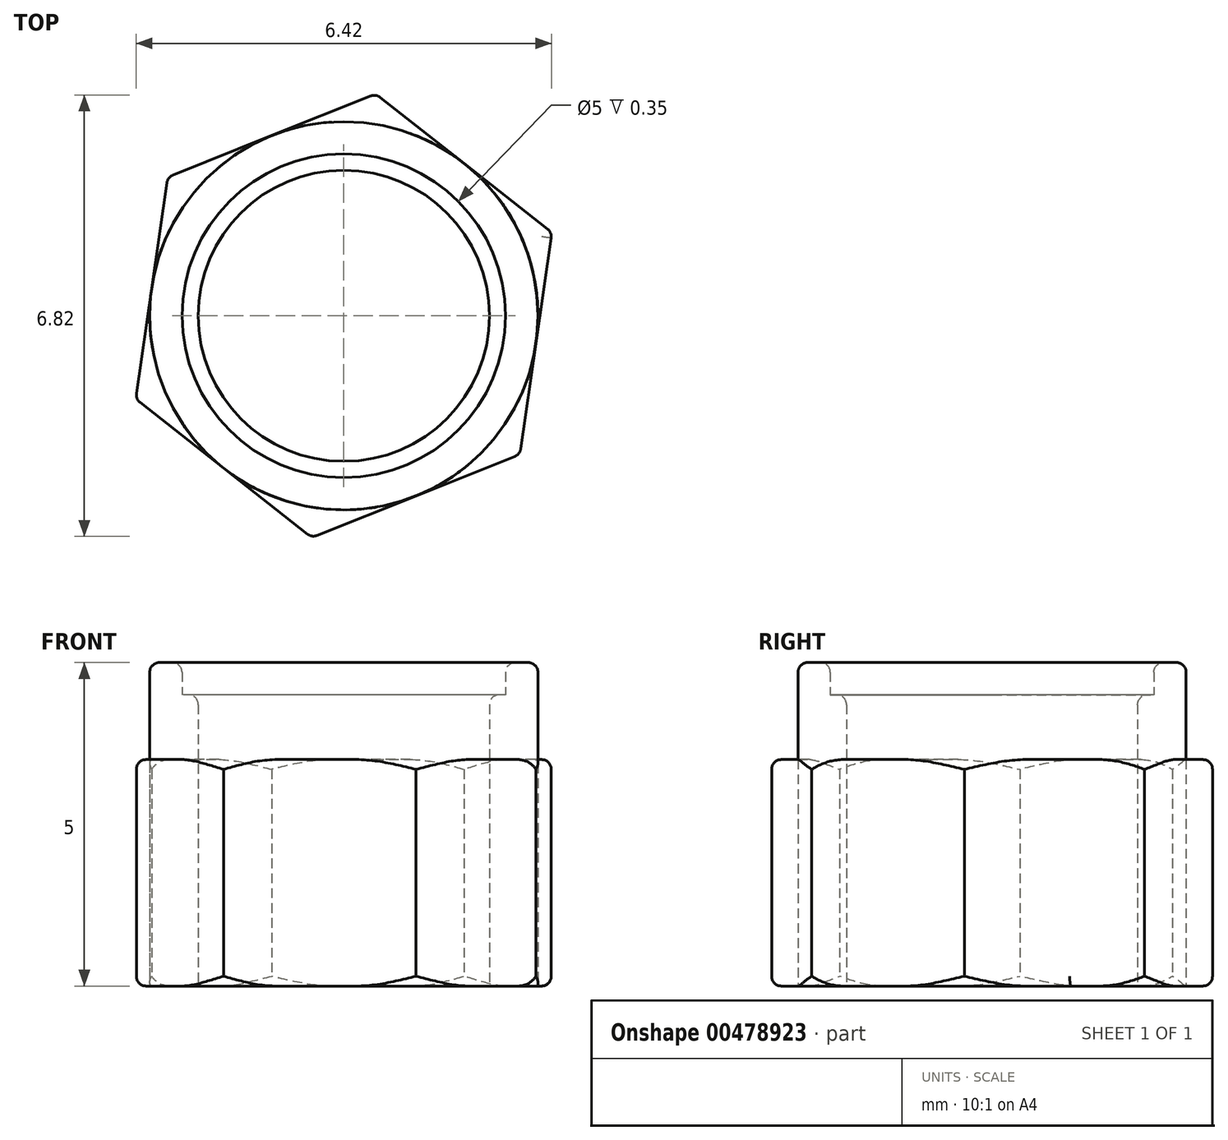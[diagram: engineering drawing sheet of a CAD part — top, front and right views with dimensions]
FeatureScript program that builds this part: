
annotation { "Feature Type Name" : "Feature", "Feature Type Description" : "" }
export const myFeature = defineFeature(function(context is Context, id is Id, definition is map)
    precondition{}
    {
        {
            var Q0;
            Q0=qCreatedBy(makeId("Top.planeOp"),FACE);
            var sketch = newSketch(context, id + "F0", { "sketchPlane" : qUnion([Q0])});
            skCircle(sketch, "E0", {"center": v(0, 0) * mm, "radius": 2.5 * mm});
            skCircle(sketch, "E1", {"center": v(0, 0) * mm, "radius": 3 * mm});
            skCircle(sketch, "E2.cCircle", {"center": v(0, 0) * mm, "radius": 3 * mm, "construction": true});
            skLineSegment(sketch, "E2.0", {"start": v(3.22, 1.29) * mm, "end": v(2.72, -2.14) * mm});
            skLineSegment(sketch, "E2.1", {"start": v(2.72, -2.14) * mm, "end": v(-0.5, -3.43) * mm});
            skLineSegment(sketch, "E2.2", {"start": v(-0.5, -3.43) * mm, "end": v(-3.22, -1.29) * mm});
            skLineSegment(sketch, "E2.3", {"start": v(-3.22, -1.29) * mm, "end": v(-2.72, 2.14) * mm});
            skLineSegment(sketch, "E2.4", {"start": v(-2.72, 2.14) * mm, "end": v(0.5, 3.43) * mm});
            skLineSegment(sketch, "E2.5", {"start": v(0.5, 3.43) * mm, "end": v(3.22, 1.29) * mm});
            skPoint(sketch, "E2.0.midPoint", {"position": v(2.97, -0.43) * mm});
            skCircle(sketch, "E3", {"center": v(0, 0) * mm, "radius": 2.25 * mm});
            skSolve(sketch);
        }
        {
            var Q0;
            {var subQ0=sQuery(id+"F0.wireOp",EDGE,"E2.4");var subQ1=sQuery(id+"F0.wireOp",EDGE,"E1");var subQ2=makeQuery(id+"F0.imprint","INTERSECT",VERTEX,{"derivedFrom":[subQ1,subQ0]});Q0=makeQuery(id+"F0.imprint","IMPRINT",FACE,{"disambiguationData":[TD([[makeQuery(id+"F0.imprint","IMPRINT",EDGE,{"disambiguationData":[TD([[subQ2,1.0]])],"derivedFrom":subQ1}),-1.0]])]});}
            var Q1;
            {var subQ0=sQuery(id+"F0.wireOp",EDGE,"E2.4");var subQ1=sQuery(id+"F0.wireOp",EDGE,"E1");var subQ2=makeQuery(id+"F0.imprint","INTERSECT",VERTEX,{"derivedFrom":[subQ1,subQ0]});Q1=makeQuery(id+"F0.imprint","IMPRINT",FACE,{"disambiguationData":[TD([[makeQuery(id+"F0.imprint","IMPRINT",EDGE,{"disambiguationData":[TD([[subQ2,-1.0]])],"derivedFrom":subQ1}),-1.0]])]});}
            var Q2;
            {var subQ0=sQuery(id+"F0.wireOp",EDGE,"E2.3");var subQ1=sQuery(id+"F0.wireOp",EDGE,"E1");var subQ2=makeQuery(id+"F0.imprint","INTERSECT",VERTEX,{"derivedFrom":[subQ1,subQ0]});Q2=makeQuery(id+"F0.imprint","IMPRINT",FACE,{"disambiguationData":[TD([[makeQuery(id+"F0.imprint","IMPRINT",EDGE,{"disambiguationData":[TD([[subQ2,-1.0]])],"derivedFrom":subQ1}),-1.0]])]});}
            var Q3;
            {var subQ0=sQuery(id+"F0.wireOp",EDGE,"E2.2");var subQ1=sQuery(id+"F0.wireOp",EDGE,"E1");var subQ2=makeQuery(id+"F0.imprint","INTERSECT",VERTEX,{"derivedFrom":[subQ1,subQ0]});Q3=makeQuery(id+"F0.imprint","IMPRINT",FACE,{"disambiguationData":[TD([[makeQuery(id+"F0.imprint","IMPRINT",EDGE,{"disambiguationData":[TD([[subQ2,-1.0]])],"derivedFrom":subQ1}),-1.0]])]});}
            var Q4;
            {var subQ0=sQuery(id+"F0.wireOp",EDGE,"E2.1");var subQ1=sQuery(id+"F0.wireOp",EDGE,"E1");var subQ2=makeQuery(id+"F0.imprint","INTERSECT",VERTEX,{"derivedFrom":[subQ1,subQ0]});Q4=makeQuery(id+"F0.imprint","IMPRINT",FACE,{"disambiguationData":[TD([[makeQuery(id+"F0.imprint","IMPRINT",EDGE,{"disambiguationData":[TD([[subQ2,-1.0]])],"derivedFrom":subQ1}),-1.0]])]});}
            var Q5;
            {var subQ0=sQuery(id+"F0.wireOp",EDGE,"E2.5");var subQ1=sQuery(id+"F0.wireOp",EDGE,"E1");var subQ2=makeQuery(id+"F0.imprint","INTERSECT",VERTEX,{"derivedFrom":[subQ1,subQ0]});Q5=makeQuery(id+"F0.imprint","IMPRINT",FACE,{"disambiguationData":[TD([[makeQuery(id+"F0.imprint","IMPRINT",EDGE,{"disambiguationData":[TD([[subQ2,1.0]])],"derivedFrom":subQ1}),-1.0]])]});}
            extrude(context, id + "F1", {"entities" : qUnion([Q0, Q1, Q2, Q3, Q4, Q5]), "depth" : 3.5 * mm, "offsetDistance" : 25 * mm});
        }
        {
            var Q0;
            Q0=makeQuery(id+"F0.imprint","IMPRINT",FACE,{"disambiguationData":[TD([[makeQuery(id+"F0.imprint","IMPRINT",EDGE,{"derivedFrom":sQuery(id+"F0.wireOp",EDGE,"E0")}),-1.0]])]});
            extrude(context, id + "F2", {"entities" : qUnion([Q0]), "depth" : 5 * mm, "offsetDistance" : 25 * mm});
        }
        {
            var Q0;
            Q0=makeQuery(id+"F0.imprint","IMPRINT",FACE,{"disambiguationData":[TD([[makeQuery(id+"F0.imprint","IMPRINT",EDGE,{"derivedFrom":sQuery(id+"F0.wireOp",EDGE,"E0")}),1.0]])]});
            extrude(context, id + "F3", {"entities" : qUnion([Q0]), "operationType" : NewBodyOperationType.ADD, "depth" : 4.5 * mm, "offsetDistance" : 25 * mm});
        }
        {
            var Q0;
            Q0=makeQuery(id+"F2.opExtrude","CAP_EDGE",EDGE,{"disambiguationData":[OSD([sQuery(id+"F0.wireOp",EDGE,"E1")])],"isStart":false});
            var Q1;
            Q1=makeQuery(id+"F1.opExtrude","SWEPT_EDGE",EDGE,{"disambiguationData":[OSD([sQuery(id+"F0.wireOp",EDGE,"E2.0"),sQuery(id+"F0.wireOp",EDGE,"E2.1")])]});
            var Q2;
            Q2=makeQuery(id+"F1.opExtrude","SWEPT_EDGE",EDGE,{"disambiguationData":[OSD([sQuery(id+"F0.wireOp",EDGE,"E2.1"),sQuery(id+"F0.wireOp",EDGE,"E2.2")])]});
            var Q3;
            Q3=makeQuery(id+"F1.opExtrude","SWEPT_EDGE",EDGE,{"disambiguationData":[OSD([sQuery(id+"F0.wireOp",EDGE,"E2.2"),sQuery(id+"F0.wireOp",EDGE,"E2.3")])]});
            var Q4;
            Q4=makeQuery(id+"F1.opExtrude","SWEPT_EDGE",EDGE,{"disambiguationData":[OSD([sQuery(id+"F0.wireOp",EDGE,"E2.0"),sQuery(id+"F0.wireOp",EDGE,"E2.5")])]});
            var Q5;
            Q5=makeQuery(id+"F1.opExtrude","SWEPT_EDGE",EDGE,{"disambiguationData":[OSD([sQuery(id+"F0.wireOp",EDGE,"E2.4"),sQuery(id+"F0.wireOp",EDGE,"E2.5")])]});
            var Q6;
            Q6=makeQuery(id+"F1.opExtrude","SWEPT_EDGE",EDGE,{"disambiguationData":[OSD([sQuery(id+"F0.wireOp",EDGE,"E2.3"),sQuery(id+"F0.wireOp",EDGE,"E2.4")])]});
            var Q7;
            {var subQ0=sQuery(id+"F0.wireOp",EDGE,"E2.3");Q7=makeQuery(id+"F1.opExtrude","CAP_EDGE",EDGE,{"disambiguationData":[OSD([subQ0]),TDD([makeQuery(id+"F0.imprint","IMPRINT",EDGE,{"disambiguationData":[TD([[makeQuery(id+"F0.imprint","INTERSECT",VERTEX,{"derivedFrom":[subQ0,sQuery(id+"F0.wireOp",EDGE,"E2.4")]}),1.0]])],"derivedFrom":subQ0})])],"isStart":false});}
            var Q8;
            {var subQ0=sQuery(id+"F0.wireOp",EDGE,"E2.4");Q8=makeQuery(id+"F1.opExtrude","CAP_EDGE",EDGE,{"disambiguationData":[OSD([subQ0]),TDD([makeQuery(id+"F0.imprint","IMPRINT",EDGE,{"disambiguationData":[TD([[makeQuery(id+"F0.imprint","INTERSECT",VERTEX,{"derivedFrom":[sQuery(id+"F0.wireOp",EDGE,"E2.3"),subQ0]}),-1.0]])],"derivedFrom":subQ0})])],"isStart":false});}
            var Q9;
            {var subQ0=sQuery(id+"F0.wireOp",EDGE,"E2.4");Q9=makeQuery(id+"F1.opExtrude","CAP_EDGE",EDGE,{"disambiguationData":[OSD([subQ0]),TDD([makeQuery(id+"F0.imprint","IMPRINT",EDGE,{"disambiguationData":[TD([[makeQuery(id+"F0.imprint","INTERSECT",VERTEX,{"derivedFrom":[subQ0,sQuery(id+"F0.wireOp",EDGE,"E2.5")]}),1.0]])],"derivedFrom":subQ0})])],"isStart":false});}
            var Q10;
            {var subQ0=sQuery(id+"F0.wireOp",EDGE,"E2.5");Q10=makeQuery(id+"F1.opExtrude","CAP_EDGE",EDGE,{"disambiguationData":[OSD([subQ0]),TDD([makeQuery(id+"F0.imprint","IMPRINT",EDGE,{"disambiguationData":[TD([[makeQuery(id+"F0.imprint","INTERSECT",VERTEX,{"derivedFrom":[sQuery(id+"F0.wireOp",EDGE,"E2.4"),subQ0]}),-1.0]])],"derivedFrom":subQ0})])],"isStart":false});}
            var Q11;
            {var subQ0=sQuery(id+"F0.wireOp",EDGE,"E2.0");Q11=makeQuery(id+"F1.opExtrude","CAP_EDGE",EDGE,{"disambiguationData":[OSD([subQ0]),TDD([makeQuery(id+"F0.imprint","IMPRINT",EDGE,{"disambiguationData":[TD([[makeQuery(id+"F0.imprint","INTERSECT",VERTEX,{"derivedFrom":[subQ0,sQuery(id+"F0.wireOp",EDGE,"E2.5")]}),-1.0]])],"derivedFrom":subQ0})])],"isStart":false});}
            var Q12;
            {var subQ0=sQuery(id+"F0.wireOp",EDGE,"E2.5");Q12=makeQuery(id+"F1.opExtrude","CAP_EDGE",EDGE,{"disambiguationData":[OSD([subQ0]),TDD([makeQuery(id+"F0.imprint","IMPRINT",EDGE,{"disambiguationData":[TD([[makeQuery(id+"F0.imprint","INTERSECT",VERTEX,{"derivedFrom":[sQuery(id+"F0.wireOp",EDGE,"E2.0"),subQ0]}),1.0]])],"derivedFrom":subQ0})])],"isStart":false});}
            var Q13;
            {var subQ0=sQuery(id+"F0.wireOp",EDGE,"E2.0");Q13=makeQuery(id+"F1.opExtrude","CAP_EDGE",EDGE,{"disambiguationData":[OSD([subQ0]),TDD([makeQuery(id+"F0.imprint","IMPRINT",EDGE,{"disambiguationData":[TD([[makeQuery(id+"F0.imprint","INTERSECT",VERTEX,{"derivedFrom":[subQ0,sQuery(id+"F0.wireOp",EDGE,"E2.1")]}),1.0]])],"derivedFrom":subQ0})])],"isStart":false});}
            var Q14;
            {var subQ0=sQuery(id+"F0.wireOp",EDGE,"E2.1");Q14=makeQuery(id+"F1.opExtrude","CAP_EDGE",EDGE,{"disambiguationData":[OSD([subQ0]),TDD([makeQuery(id+"F0.imprint","IMPRINT",EDGE,{"disambiguationData":[TD([[makeQuery(id+"F0.imprint","INTERSECT",VERTEX,{"derivedFrom":[sQuery(id+"F0.wireOp",EDGE,"E2.0"),subQ0]}),-1.0]])],"derivedFrom":subQ0})])],"isStart":false});}
            var Q15;
            {var subQ0=sQuery(id+"F0.wireOp",EDGE,"E2.1");Q15=makeQuery(id+"F1.opExtrude","CAP_EDGE",EDGE,{"disambiguationData":[OSD([subQ0]),TDD([makeQuery(id+"F0.imprint","IMPRINT",EDGE,{"disambiguationData":[TD([[makeQuery(id+"F0.imprint","INTERSECT",VERTEX,{"derivedFrom":[subQ0,sQuery(id+"F0.wireOp",EDGE,"E2.2")]}),1.0]])],"derivedFrom":subQ0})])],"isStart":false});}
            var Q16;
            {var subQ0=sQuery(id+"F0.wireOp",EDGE,"E2.2");Q16=makeQuery(id+"F1.opExtrude","CAP_EDGE",EDGE,{"disambiguationData":[OSD([subQ0]),TDD([makeQuery(id+"F0.imprint","IMPRINT",EDGE,{"disambiguationData":[TD([[makeQuery(id+"F0.imprint","INTERSECT",VERTEX,{"derivedFrom":[sQuery(id+"F0.wireOp",EDGE,"E2.1"),subQ0]}),-1.0]])],"derivedFrom":subQ0})])],"isStart":false});}
            var Q17;
            {var subQ0=sQuery(id+"F0.wireOp",EDGE,"E2.2");Q17=makeQuery(id+"F1.opExtrude","CAP_EDGE",EDGE,{"disambiguationData":[OSD([subQ0]),TDD([makeQuery(id+"F0.imprint","IMPRINT",EDGE,{"disambiguationData":[TD([[makeQuery(id+"F0.imprint","INTERSECT",VERTEX,{"derivedFrom":[subQ0,sQuery(id+"F0.wireOp",EDGE,"E2.3")]}),1.0]])],"derivedFrom":subQ0})])],"isStart":false});}
            var Q18;
            {var subQ0=sQuery(id+"F0.wireOp",EDGE,"E2.3");Q18=makeQuery(id+"F1.opExtrude","CAP_EDGE",EDGE,{"disambiguationData":[OSD([subQ0]),TDD([makeQuery(id+"F0.imprint","IMPRINT",EDGE,{"disambiguationData":[TD([[makeQuery(id+"F0.imprint","INTERSECT",VERTEX,{"derivedFrom":[sQuery(id+"F0.wireOp",EDGE,"E2.2"),subQ0]}),-1.0]])],"derivedFrom":subQ0})])],"isStart":false});}
            fillet(context, id + "F4", {"entities" : qUnion([Q0, Q1, Q2, Q3, Q4, Q5, Q6, Q7, Q8, Q9, Q10, Q11, Q12, Q13, Q14, Q15, Q16, Q17, Q18]), "radius" : .15 * mm, "tangentPropagation" : true, "allowEdgeOverflow" : false});
        }
        {
            var Q0;
            Q0=makeQuery(id+"F3.opExtrude","CAP_EDGE",EDGE,{"disambiguationData":[OSD([sQuery(id+"F0.wireOp",EDGE,"E3")])],"isStart":false});
            var Q1;
            Q1=makeQuery(id+"F2.opExtrude","CAP_EDGE",EDGE,{"disambiguationData":[OSD([sQuery(id+"F0.wireOp",EDGE,"E0")])],"isStart":false});
            var Q2;
            {var subQ0=sQuery(id+"F0.wireOp",EDGE,"E2.3");Q2=makeQuery(id+"F1.opExtrude","CAP_EDGE",EDGE,{"disambiguationData":[OSD([subQ0]),TDD([makeQuery(id+"F0.imprint","IMPRINT",EDGE,{"disambiguationData":[TD([[makeQuery(id+"F0.imprint","INTERSECT",VERTEX,{"derivedFrom":[subQ0,sQuery(id+"F0.wireOp",EDGE,"E2.4")]}),1.0]])],"derivedFrom":subQ0})])],"isStart":true});}
            var Q3;
            {var subQ0=sQuery(id+"F0.wireOp",EDGE,"E2.3");Q3=makeQuery(id+"F1.opExtrude","CAP_EDGE",EDGE,{"disambiguationData":[OSD([subQ0]),TDD([makeQuery(id+"F0.imprint","IMPRINT",EDGE,{"disambiguationData":[TD([[makeQuery(id+"F0.imprint","INTERSECT",VERTEX,{"derivedFrom":[sQuery(id+"F0.wireOp",EDGE,"E2.2"),subQ0]}),-1.0]])],"derivedFrom":subQ0})])],"isStart":true});}
            var Q4;
            {var subQ0=sQuery(id+"F0.wireOp",EDGE,"E2.2");Q4=makeQuery(id+"F1.opExtrude","CAP_EDGE",EDGE,{"disambiguationData":[OSD([subQ0]),TDD([makeQuery(id+"F0.imprint","IMPRINT",EDGE,{"disambiguationData":[TD([[makeQuery(id+"F0.imprint","INTERSECT",VERTEX,{"derivedFrom":[sQuery(id+"F0.wireOp",EDGE,"E2.1"),subQ0]}),-1.0]])],"derivedFrom":subQ0})])],"isStart":true});}
            var Q5;
            {var subQ0=sQuery(id+"F0.wireOp",EDGE,"E2.1");Q5=makeQuery(id+"F1.opExtrude","CAP_EDGE",EDGE,{"disambiguationData":[OSD([subQ0]),TDD([makeQuery(id+"F0.imprint","IMPRINT",EDGE,{"disambiguationData":[TD([[makeQuery(id+"F0.imprint","INTERSECT",VERTEX,{"derivedFrom":[sQuery(id+"F0.wireOp",EDGE,"E2.0"),subQ0]}),-1.0]])],"derivedFrom":subQ0})])],"isStart":true});}
            var Q6;
            {var subQ0=sQuery(id+"F0.wireOp",EDGE,"E2.0");Q6=makeQuery(id+"F1.opExtrude","CAP_EDGE",EDGE,{"disambiguationData":[OSD([subQ0]),TDD([makeQuery(id+"F0.imprint","IMPRINT",EDGE,{"disambiguationData":[TD([[makeQuery(id+"F0.imprint","INTERSECT",VERTEX,{"derivedFrom":[subQ0,sQuery(id+"F0.wireOp",EDGE,"E2.5")]}),-1.0]])],"derivedFrom":subQ0})])],"isStart":true});}
            var Q7;
            {var subQ0=sQuery(id+"F0.wireOp",EDGE,"E2.5");Q7=makeQuery(id+"F1.opExtrude","CAP_EDGE",EDGE,{"disambiguationData":[OSD([subQ0]),TDD([makeQuery(id+"F0.imprint","IMPRINT",EDGE,{"disambiguationData":[TD([[makeQuery(id+"F0.imprint","INTERSECT",VERTEX,{"derivedFrom":[sQuery(id+"F0.wireOp",EDGE,"E2.4"),subQ0]}),-1.0]])],"derivedFrom":subQ0})])],"isStart":true});}
            fillet(context, id + "F5", {"entities" : qUnion([Q0, Q1, Q2, Q3, Q4, Q5, Q6, Q7]), "radius" : .15 * mm, "tangentPropagation" : true, "allowEdgeOverflow" : false});
        }
    });
